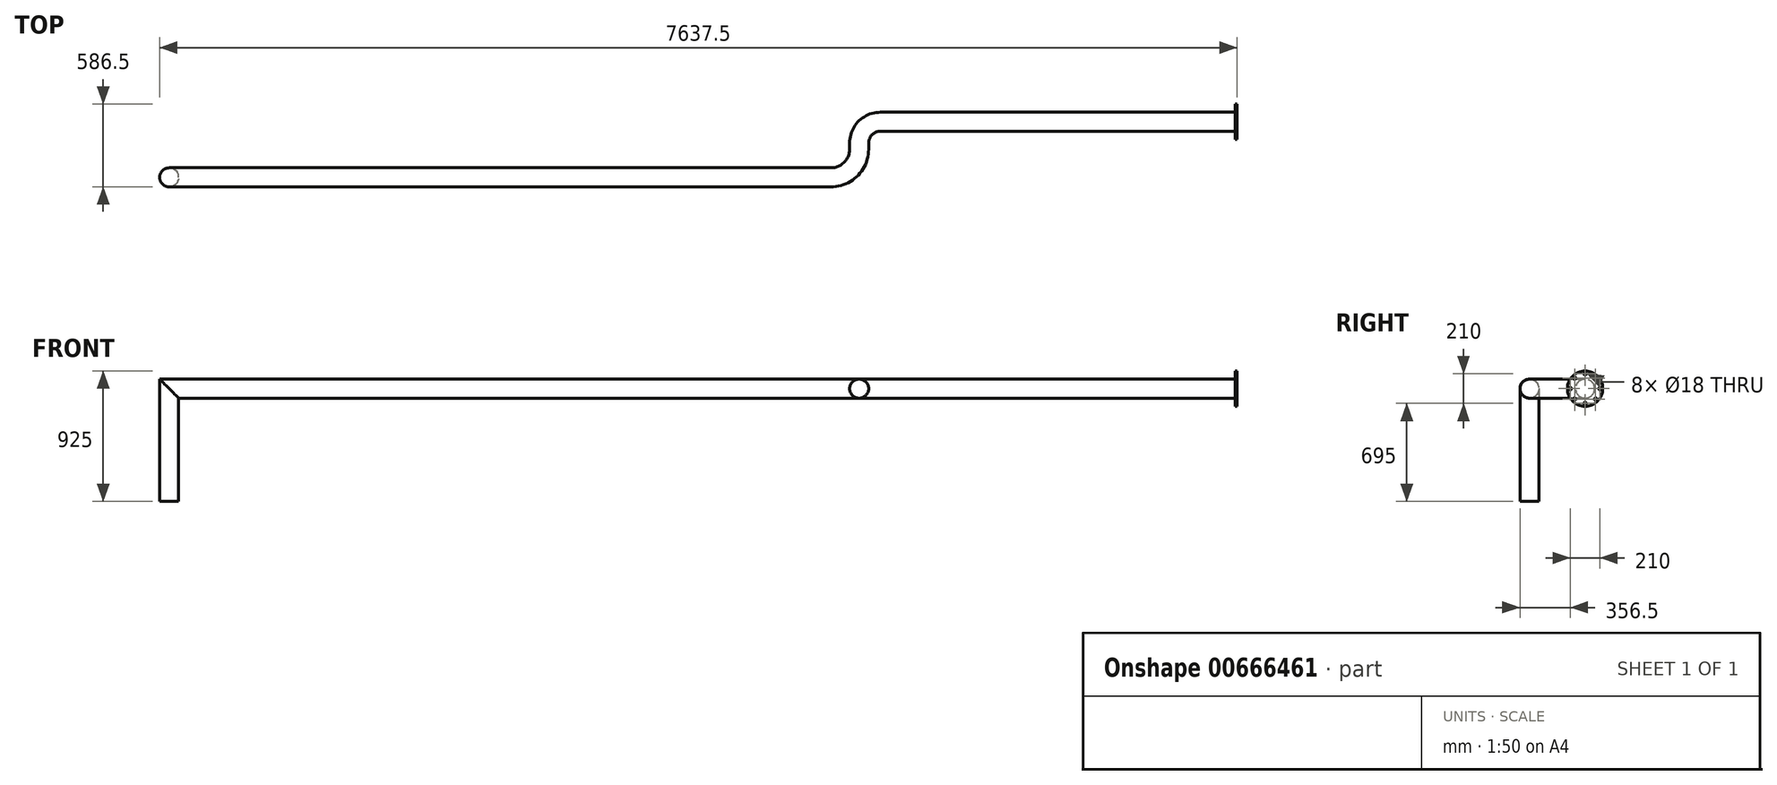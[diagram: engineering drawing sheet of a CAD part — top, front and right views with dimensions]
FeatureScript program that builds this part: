
annotation { "Feature Type Name" : "Feature", "Feature Type Description" : "" }
export const myFeature = defineFeature(function(context is Context, id is Id, definition is map)
    precondition{}
    {
        {
            var Q0;
            Q0=qCreatedBy(makeId("Top.planeOp"),FACE);
            var sketch = newSketch(context, id + "F0", { "sketchPlane" : qUnion([Q0])});
            skLineSegment(sketch, "E0", {"start": v(2619.9, 394) * mm, "end": v(5150, 394) * mm});
            skPoint(sketch, "E1.visualSharp", {"position": v(0, 394) * mm});
            skLineSegment(sketch, "E2", {"start": v(0, 0) * mm, "end": v(2269.9, 0) * mm});
            skLineSegment(sketch, "E3", {"start": v(2469.9, 200) * mm, "end": v(2469.9, 244) * mm});
            skPoint(sketch, "E4.visualSharp", {"position": v(2469.9, 0) * mm});
            skArc(sketch, "E4.filletArc", {"start": v(2269.9, 0) * mm, "mid": v(2411.33, 58.58) * mm, "end": v(2469.9, 200) * mm});
            skPoint(sketch, "E5.visualSharp", {"position": v(2469.9, 394) * mm});
            skArc(sketch, "E5.filletArc", {"start": v(2619.9, 394) * mm, "mid": v(2513.84, 350.07) * mm, "end": v(2469.9, 244) * mm});
            skLineSegment(sketch, "E6", {"start": v(0, 0) * mm, "end": v(-2420, 0) * mm});
            skSolve(sketch);
        }
        {
            var Q0;
            Q0=qCreatedBy(makeId("Front.planeOp"),FACE);
            var sketch = newSketch(context, id + "F1", { "sketchPlane" : qUnion([Q0])});
            skPoint(sketch, "E7.0", {"position": v(-2420, 0) * mm});
            skLineSegment(sketch, "E8", {"start": v(-2420, 0) * mm, "end": v(-2420, -800) * mm});
            skSolve(sketch);
        }
        {
            var Q0;
            Q0=qCreatedBy(makeId("Right.planeOp"),FACE);
            cPlane(context, id + "F2", {"entities" : qUnion([Q0]), "cplaneType" : CPlaneType.OFFSET, "offset" : 5150 * mm, "width" : 150 * mm, "height" : 150 * mm});
        }
        {
            var Q0;
            Q0=qCreatedBy(id+"F2.planeOp",FACE);
            var sketch = newSketch(context, id + "F3", { "sketchPlane" : qUnion([Q0])});
            skPoint(sketch, "E9.0", {"position": v(394, 0) * mm});
            skCircle(sketch, "E10", {"center": v(394, 0) * mm, "radius": 67.5 * mm});
            skCircle(sketch, "E11", {"center": v(394, 0) * mm, "radius": 125 * mm});
            skCircle(sketch, "E12", {"center": v(289, 0) * mm, "radius": 9 * mm});
            skCircle(sketch, "E13.1.0", {"center": v(319.75, -74.25) * mm, "radius": 9 * mm});
            skCircle(sketch, "E13.2.0", {"center": v(394, -105) * mm, "radius": 9 * mm});
            skCircle(sketch, "E13.3.0", {"center": v(468.25, -74.25) * mm, "radius": 9 * mm});
            skCircle(sketch, "E13.4.0", {"center": v(499, 0) * mm, "radius": 9 * mm});
            skCircle(sketch, "E13.5.0", {"center": v(468.25, 74.25) * mm, "radius": 9 * mm});
            skCircle(sketch, "E13.6.0", {"center": v(394, 105) * mm, "radius": 9 * mm});
            skCircle(sketch, "E13.7.0", {"center": v(319.75, 74.25) * mm, "radius": 9 * mm});
            skSolve(sketch);
        }
        {
            var Q0;
            Q0=makeQuery(id+"F3.imprint","IMPRINT",FACE,{"disambiguationData":[TD([[makeQuery(id+"F3.imprint","IMPRINT",EDGE,{"derivedFrom":sQuery(id+"F3.wireOp",EDGE,"E10")}),1.0]])]});
            var Q1;
            Q1=sQuery(id+"F0.wireOp",EDGE,"E0");
            var Q2;
            Q2=sQuery(id+"F0.wireOp",EDGE,"E5.filletArc");
            var Q3;
            Q3=sQuery(id+"F0.wireOp",EDGE,"E3");
            var Q4;
            Q4=sQuery(id+"F0.wireOp",EDGE,"E4.filletArc");
            var Q5;
            Q5=sQuery(id+"F0.wireOp",EDGE,"E2");
            var Q6;
            Q6=sQuery(id+"F0.wireOp",EDGE,"E6");
            var Q7;
            Q7=sQuery(id+"F1.wireOp",EDGE,"E8");
            sweep(context, id + "F4", {"profiles" : qUnion([Q0]), "path" : qUnion([Q1, Q2, Q3, Q4, Q5, Q6, Q7])});
        }
        {
            var Q0;
            Q0=makeQuery(id+"F3.imprint","IMPRINT",FACE,{"disambiguationData":[TD([[makeQuery(id+"F3.imprint","IMPRINT",EDGE,{"derivedFrom":sQuery(id+"F3.wireOp",EDGE,"E10")}),-1.0]])]});
            extrude(context, id + "F5", {"entities" : qUnion([Q0]), "operationType" : NewBodyOperationType.ADD, "oppositeDirection" : true, "depth" : 15 * mm, "offsetDistance" : 25 * mm});
        }
    });
